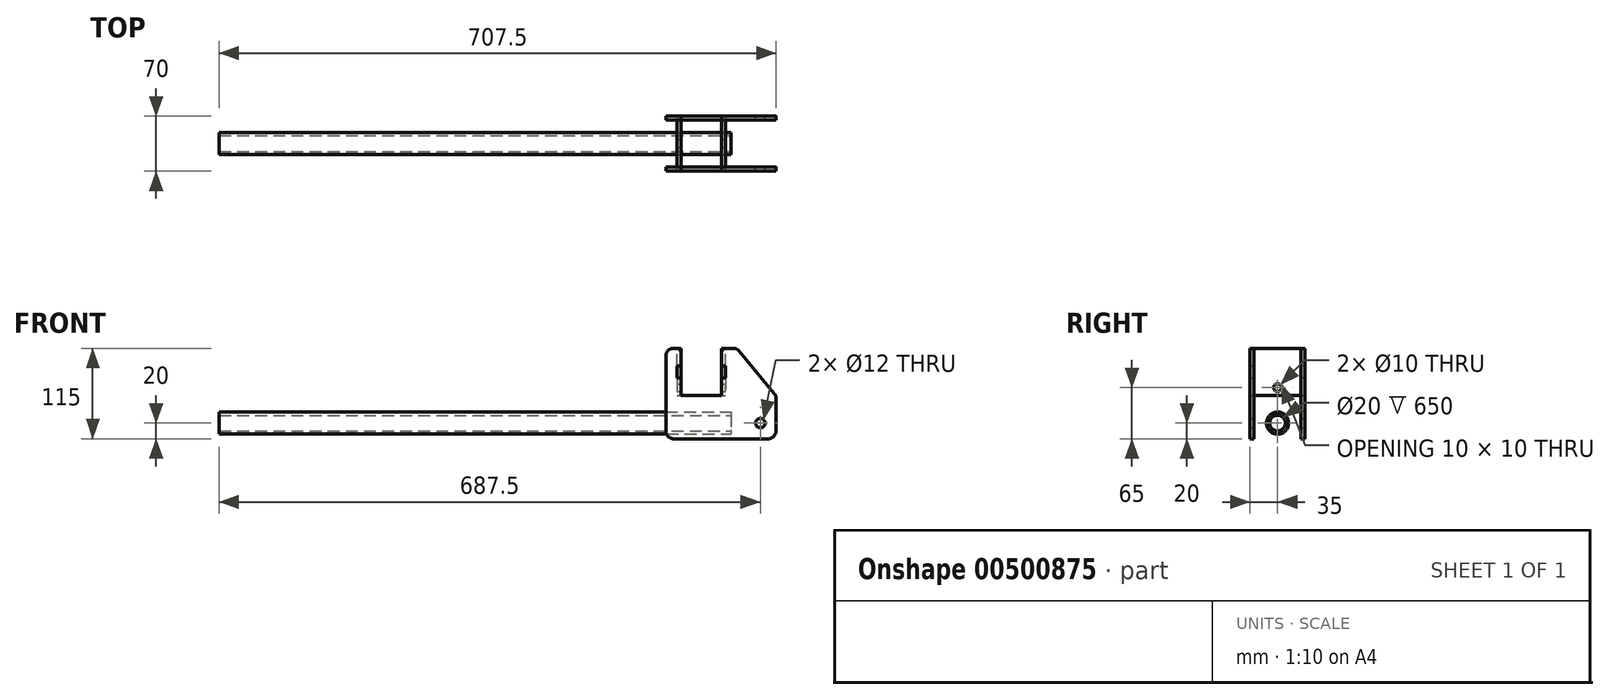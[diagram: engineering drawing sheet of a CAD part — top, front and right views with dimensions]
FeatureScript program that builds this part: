
annotation { "Feature Type Name" : "Feature", "Feature Type Description" : "" }
export const myFeature = defineFeature(function(context is Context, id is Id, definition is map)
    precondition{}
    {
        {
            var Q0;
            Q0=qCreatedBy(makeId("Front.planeOp"),FACE);
            var sketch = newSketch(context, id + "F0", { "sketchPlane" : qUnion([Q0])});
            skLineSegment(sketch, "E0", {"start": v(10, 0) * mm, "end": v(130, 0) * mm});
            skLineSegment(sketch, "E1", {"start": v(0, 10) * mm, "end": v(0, 105) * mm});
            skLineSegment(sketch, "E2", {"start": v(10, 115) * mm, "end": v(14, 115) * mm});
            skLineSegment(sketch, "E3", {"start": v(93, 111.4) * mm, "end": v(137.68, 57.78) * mm});
            skLineSegment(sketch, "E4", {"start": v(140, 51.38) * mm, "end": v(140, 10) * mm});
            skPoint(sketch, "E5", {"position": v(19, 55) * mm});
            skPoint(sketch, "E6", {"position": v(45, 115) * mm});
            skLineSegment(sketch, "E7", {"start": v(19, 55) * mm, "end": v(19, 110) * mm});
            skLineSegment(sketch, "E8", {"start": v(19, 55) * mm, "end": v(71, 55) * mm});
            skLineSegment(sketch, "E9", {"start": v(71, 55) * mm, "end": v(71, 110) * mm});
            skPoint(sketch, "E10", {"position": v(19, 85) * mm});
            skLineSegment(sketch, "E11", {"start": v(19, 85) * mm, "end": v(19, 92.5) * mm});
            skLineSegment(sketch, "E12", {"start": v(19, 92.5) * mm, "end": v(14, 92.5) * mm});
            skLineSegment(sketch, "E13", {"start": v(14, 92.5) * mm, "end": v(14, 77.5) * mm});
            skLineSegment(sketch, "E14", {"start": v(14, 77.5) * mm, "end": v(19, 77.5) * mm});
            skLineSegment(sketch, "E15", {"start": v(45, 115) * mm, "end": v(45, 55) * mm, "construction": true});
            skLineSegment(sketch, "E16.MirrorCS", {"start": v(71, 92.5) * mm, "end": v(76, 92.5) * mm});
            skLineSegment(sketch, "E17.MirrorCS", {"start": v(76, 92.5) * mm, "end": v(76, 77.5) * mm});
            skLineSegment(sketch, "E18.MirrorCS", {"start": v(76, 77.5) * mm, "end": v(71, 77.5) * mm});
            skPoint(sketch, "E19.visualSharp", {"position": v(90, 115) * mm});
            skArc(sketch, "E19.filletArc", {"start": v(93, 111.4) * mm, "mid": v(89.56, 114.06) * mm, "end": v(85.32, 115) * mm});
            skPoint(sketch, "E20.visualSharp", {"position": v(0, 115) * mm});
            skArc(sketch, "E20.filletArc", {"start": v(10, 115) * mm, "mid": v(2.93, 112.07) * mm, "end": v(0, 105) * mm});
            skPoint(sketch, "E21.visualSharp", {"position": v(0, 0) * mm});
            skArc(sketch, "E21.filletArc", {"start": v(0, 10) * mm, "mid": v(2.93, 2.93) * mm, "end": v(10, 0) * mm});
            skPoint(sketch, "E22.visualSharp", {"position": v(140, 0) * mm});
            skArc(sketch, "E22.filletArc", {"start": v(130, 0) * mm, "mid": v(137.07, 2.93) * mm, "end": v(140, 10) * mm});
            skPoint(sketch, "E23.visualSharp", {"position": v(140, 55) * mm});
            skArc(sketch, "E23.filletArc", {"start": v(140, 51.38) * mm, "mid": v(139.4, 54.78) * mm, "end": v(137.68, 57.78) * mm});
            skPoint(sketch, "E24", {"position": v(120, 20) * mm});
            skCircle(sketch, "E25", {"center": v(120, 20) * mm, "radius": 6 * mm});
            skLineSegment(sketch, "E26.trimOffspring", {"start": v(76, 115) * mm, "end": v(85.32, 115) * mm});
            skPoint(sketch, "E27.visualSharp", {"position": v(19, 115) * mm});
            skArc(sketch, "E27.filletArc", {"start": v(19, 110) * mm, "mid": v(17.54, 113.54) * mm, "end": v(14, 115) * mm});
            skPoint(sketch, "E28.visualSharp", {"position": v(71, 115) * mm});
            skArc(sketch, "E28.filletArc", {"start": v(76, 115) * mm, "mid": v(72.46, 113.54) * mm, "end": v(71, 110) * mm});
            skSolve(sketch);
        }
        {
            var Q0;
            Q0=makeQuery(id+"F0.imprint","IMPRINT",FACE,{"disambiguationData":[TD([[makeQuery(id+"F0.imprint","IMPRINT",EDGE,{"derivedFrom":sQuery(id+"F0.wireOp",EDGE,"E0")}),1.0]])]});
            extrude(context, id + "F1", {"entities" : qUnion([Q0]), "depth" : 5 * mm});
        }
        {
            var Q0;
            Q0=makeQuery(id+"F1.opExtrude","SWEPT_FACE",FACE,{"disambiguationData":[OSD([sQuery(id+"F0.wireOp",EDGE,"E17.MirrorCS")])]});
            var sketch = newSketch(context, id + "F2", { "sketchPlane" : qUnion([Q0])});
            skLineSegment(sketch, "E29.0", {"start": v(5, 92.5) * mm, "end": v(5, 77.5) * mm});
            skLineSegment(sketch, "E30.0.1", {"start": v(0, 92.5) * mm, "end": v(5, 92.5) * mm});
            skLineSegment(sketch, "E30.0.3", {"start": v(5, 92.5) * mm, "end": v(0, 92.5) * mm});
            skLineSegment(sketch, "E31.0", {"start": v(5, 77.5) * mm, "end": v(0, 77.5) * mm});
            skLineSegment(sketch, "E32", {"start": v(0, 92.5) * mm, "end": v(0, 115) * mm});
            skLineSegment(sketch, "E33", {"start": v(0, 115) * mm, "end": v(-60, 115) * mm});
            skLineSegment(sketch, "E34", {"start": v(-60, 115) * mm, "end": v(-60, 55) * mm});
            skLineSegment(sketch, "E35", {"start": v(-60, 55) * mm, "end": v(0, 55) * mm});
            skLineSegment(sketch, "E36", {"start": v(0, 55) * mm, "end": v(0, 77.5) * mm});
            skLineSegment(sketch, "E37", {"start": v(-30, 115) * mm, "end": v(-30, 55) * mm, "construction": true});
            skLineSegment(sketch, "E38.MirrorCS", {"start": v(-65, 92.5) * mm, "end": v(-65, 77.5) * mm});
            skLineSegment(sketch, "E39.MirrorCS", {"start": v(-65, 77.5) * mm, "end": v(-60, 77.5) * mm});
            skLineSegment(sketch, "E40.MirrorCS", {"start": v(-65, 92.5) * mm, "end": v(-60, 92.5) * mm});
            skSolve(sketch);
        }
        {
            var Q0;
            Q0=qSketchRegion(id+"F2",true);
            extrude(context, id + "F3", {"entities" : qUnion([Q0]), "depth" : 5 * mm});
        }
        {
            var Q0;
            Q0=makeQuery(id+"F3.opExtrude","CAP_FACE",FACE,{"disambiguationData":[OSD([sQuery(id+"F2.wireOp",EDGE,"E29.0"),sQuery(id+"F2.wireOp",EDGE,"E30.0.3"),sQuery(id+"F2.wireOp",EDGE,"E31.0"),sQuery(id+"F2.wireOp",EDGE,"E32"),sQuery(id+"F2.wireOp",EDGE,"E33"),sQuery(id+"F2.wireOp",EDGE,"E34"),sQuery(id+"F2.wireOp",EDGE,"E35"),sQuery(id+"F2.wireOp",EDGE,"E36"),sQuery(id+"F2.wireOp",EDGE,"E38.MirrorCS"),sQuery(id+"F2.wireOp",EDGE,"E39.MirrorCS"),sQuery(id+"F2.wireOp",EDGE,"E40.MirrorCS")])],"isStart":true});
            var sketch = newSketch(context, id + "F4", { "sketchPlane" : qUnion([Q0])});
            skPoint(sketch, "E41", {"position": v(30, 65) * mm});
            skPoint(sketch, "E41.positionSnap0", {"position": v(30, 55) * mm});
            skCircle(sketch, "E42", {"center": v(30, 65) * mm, "radius": 5 * mm});
            skSolve(sketch);
        }
        {
            var Q0;
            Q0 = qSketchRegion(id + "F4", true);
            extrude(context, id + "F5", {"entities" : qUnion([Q0]), "operationType" : NewBodyOperationType.REMOVE, "oppositeDirection" : true, "depth" : 25 * mm, "offsetDistance" : 25 * mm});
        }
        {
            var Q0;
            Q0=makeQuery(id+"F1.opExtrude","CAP_FACE",FACE,{"disambiguationData":[OSD([sQuery(id+"F0.wireOp",EDGE,"E0"),sQuery(id+"F0.wireOp",EDGE,"E1"),sQuery(id+"F0.wireOp",EDGE,"E2"),sQuery(id+"F0.wireOp",EDGE,"E3"),sQuery(id+"F0.wireOp",EDGE,"E4"),sQuery(id+"F0.wireOp",EDGE,"E7"),sQuery(id+"F0.wireOp",EDGE,"E8"),sQuery(id+"F0.wireOp",EDGE,"E9"),sQuery(id+"F0.wireOp",EDGE,"E12"),sQuery(id+"F0.wireOp",EDGE,"E13"),sQuery(id+"F0.wireOp",EDGE,"E14"),sQuery(id+"F0.wireOp",EDGE,"E16.MirrorCS"),sQuery(id+"F0.wireOp",EDGE,"E17.MirrorCS"),sQuery(id+"F0.wireOp",EDGE,"E18.MirrorCS"),sQuery(id+"F0.wireOp",EDGE,"E19.filletArc"),sQuery(id+"F0.wireOp",EDGE,"E20.filletArc"),sQuery(id+"F0.wireOp",EDGE,"E21.filletArc"),sQuery(id+"F0.wireOp",EDGE,"E22.filletArc"),sQuery(id+"F0.wireOp",EDGE,"E23.filletArc"),sQuery(id+"F0.wireOp",EDGE,"E25"),sQuery(id+"F0.wireOp",EDGE,"E26.trimOffspring"),sQuery(id+"F0.wireOp",EDGE,"E27.filletArc"),sQuery(id+"F0.wireOp",EDGE,"E28.filletArc")])],"isStart":true});
            cPlane(context, id + "F6", {"entities" : qUnion([Q0]), "cplaneType" : CPlaneType.OFFSET, "offset" : 10 * mm, "width" : 150 * mm, "height" : 150 * mm});
        }
        {
            var Q0;
            Q0=qCreatedBy(id+"F6.planeOp",FACE);
            var sketch = newSketch(context, id + "F7", { "sketchPlane" : qUnion([Q0])});
            skCircle(sketch, "E43.0", {"center": v(-120, 20) * mm, "radius": 6 * mm, "construction": true});
            skCircle(sketch, "E44", {"center": v(-120, 20) * mm, "radius": 26 * mm});
            skLineSegment(sketch, "E45.bottom", {"start": v(-82.5, 55) * mm, "end": v(-157.5, 55) * mm});
            skLineSegment(sketch, "E45.top", {"start": v(-82.5, -15) * mm, "end": v(-157.5, -15) * mm});
            skLineSegment(sketch, "E45.left", {"start": v(-82.5, 55) * mm, "end": v(-82.5, -15) * mm});
            skLineSegment(sketch, "E45.right", {"start": v(-157.5, 55) * mm, "end": v(-157.5, -15) * mm});
            skSolve(sketch);
        }
        {
            var Q0;
            Q0 = qSketchRegion(id + "F7", true);
            extrude(context, id + "F8", {"entities" : qUnion([Q0]), "depth" : 40 * mm, "offsetDistance" : 25 * mm});
        }
        {
            var Q0;
            Q0=makeQuery(id+"F8.opExtrude","SWEPT_FACE",FACE,{"disambiguationData":[OSD([sQuery(id+"F7.wireOp",EDGE,"E45.bottom")])]});
            var sketch = newSketch(context, id + "F9", { "sketchPlane" : qUnion([Q0])});
            skLineSegment(sketch, "E46", {"start": v(82.5, 15) * mm, "end": v(157.5, 15) * mm});
            skLineSegment(sketch, "E47", {"start": v(157.5, 15) * mm, "end": v(157.5, 45) * mm});
            skLineSegment(sketch, "E48", {"start": v(157.5, 45) * mm, "end": v(82.5, 45) * mm});
            skLineSegment(sketch, "E49", {"start": v(87.5, 15) * mm, "end": v(87.5, 45) * mm});
            skSolve(sketch);
        }
        {
            var Q0;
            Q0 = qSketchRegion(id + "F9", true);
            extrude(context, id + "F10", {"entities" : qUnion([Q0]), "operationType" : NewBodyOperationType.REMOVE, "oppositeDirection" : true, "depth" : 70 * mm, "offsetDistance" : 25 * mm});
        }
        {
            var Q0;
            Q0=makeQuery(id+"F8.opExtrude","SWEPT_EDGE",EDGE,{"disambiguationData":[OSD([sQuery(id+"F7.wireOp",EDGE,"E45.top"),sQuery(id+"F7.wireOp",EDGE,"E45.left")])]});
            var Q1;
            Q1=makeQuery(id+"F8.opExtrude","SWEPT_EDGE",EDGE,{"disambiguationData":[OSD([sQuery(id+"F7.wireOp",EDGE,"E45.bottom"),sQuery(id+"F7.wireOp",EDGE,"E45.left")])]});
            fillet(context, id + "F11", {"entities" : qUnion([Q0, Q1]), "radius" : 15 * mm, "tangentPropagation" : true, "allowEdgeOverflow" : false});
        }
        {
            var Q0;
            {var subQ0=sQuery(id+"F7.wireOp",EDGE,"E45.right");var subQ1=sQuery(id+"F7.wireOp",EDGE,"E45.bottom");Q0=makeQuery(id+"F10.boolean.opBoolean","SPLIT",EDGE,{"disambiguationData":[TD([makeQuery(id+"F10.opExtrude","SWEPT_FACE",FACE,{"disambiguationData":[OSD([sQuery(id+"F9.wireOp",EDGE,"E48")])]})])],"derivedFrom":makeQuery(id+"F8.opExtrude","SWEPT_EDGE",EDGE,{"disambiguationData":[OSD([subQ1,subQ0])]})});}
            var Q1;
            {var subQ0=sQuery(id+"F7.wireOp",EDGE,"E45.right");var subQ1=sQuery(id+"F7.wireOp",EDGE,"E45.bottom");Q1=makeQuery(id+"F10.boolean.opBoolean","SPLIT",EDGE,{"disambiguationData":[TD([makeQuery(id+"F10.opExtrude","SWEPT_FACE",FACE,{"disambiguationData":[OSD([sQuery(id+"F9.wireOp",EDGE,"E46")])]})])],"derivedFrom":makeQuery(id+"F8.opExtrude","SWEPT_EDGE",EDGE,{"disambiguationData":[OSD([subQ1,subQ0])]})});}
            var Q2;
            {var subQ0=sQuery(id+"F7.wireOp",EDGE,"E45.right");var subQ1=sQuery(id+"F7.wireOp",EDGE,"E45.top");Q2=makeQuery(id+"F10.boolean.opBoolean","SPLIT",EDGE,{"disambiguationData":[TD([makeQuery(id+"F10.opExtrude","SWEPT_FACE",FACE,{"disambiguationData":[OSD([sQuery(id+"F9.wireOp",EDGE,"E48")])]})])],"derivedFrom":makeQuery(id+"F8.opExtrude","SWEPT_EDGE",EDGE,{"disambiguationData":[OSD([subQ1,subQ0])]})});}
            var Q3;
            {var subQ0=sQuery(id+"F7.wireOp",EDGE,"E45.right");var subQ1=sQuery(id+"F7.wireOp",EDGE,"E45.top");Q3=makeQuery(id+"F10.boolean.opBoolean","SPLIT",EDGE,{"disambiguationData":[TD([makeQuery(id+"F10.opExtrude","SWEPT_FACE",FACE,{"disambiguationData":[OSD([sQuery(id+"F9.wireOp",EDGE,"E46")])]})])],"derivedFrom":makeQuery(id+"F8.opExtrude","SWEPT_EDGE",EDGE,{"disambiguationData":[OSD([subQ1,subQ0])]})});}
            fillet(context, id + "F12", {"entities" : qUnion([Q0, Q1, Q2, Q3]), "radius" : 5 * mm, "tangentPropagation" : true, "allowEdgeOverflow" : false});
        }
        {
            var Q0;
            Q0=makeQuery(id+"F8.opExtrude","SWEPT_FACE",FACE,{"disambiguationData":[OSD([sQuery(id+"F7.wireOp",EDGE,"E45.left")])]});
            var sketch = newSketch(context, id + "F13", { "sketchPlane" : qUnion([Q0])});
            skCircle(sketch, "E50", {"center": v(-30, 20) * mm, "radius": 14 * mm});
            skPoint(sketch, "E50.centerSnap0", {"position": v(-50, 20) * mm});
            skPoint(sketch, "E50.centerSnap1", {"position": v(-30, 40) * mm});
            skSolve(sketch);
        }
        {
            var Q0;
            Q0 = qSketchRegion(id + "F13", true);
            extrude(context, id + "F14", {"entities" : qUnion([Q0]), "operationType" : NewBodyOperationType.REMOVE, "oppositeDirection" : true, "depth" : 25 * mm, "offsetDistance" : 25 * mm});
        }
        {
            var Q0;
            Q0=makeQuery(id+"F8.opExtrude","SWEPT_FACE",FACE,{"disambiguationData":[OSD([sQuery(id+"F7.wireOp",EDGE,"E45.left")])]});
            var sketch = newSketch(context, id + "F15", { "sketchPlane" : qUnion([Q0])});
            skCircle(sketch, "E51.0", {"center": v(-30, 20) * mm, "radius": 14 * mm});
            skCircle(sketch, "E52", {"center": v(-30, 20) * mm, "radius": 10 * mm});
            skSolve(sketch);
        }
        {
            var Q0;
            Q0 = qSketchRegion(id + "F15", true);
            extrude(context, id + "F16", {"entities" : qUnion([Q0]), "depth" : 650 * mm, "offsetDistance" : 25 * mm});
        }
        {
            var Q0;
            Q0=makeQuery(id+"F1.opExtrude","CAP_FACE",FACE,{"disambiguationData":[OSD([sQuery(id+"F0.wireOp",EDGE,"E0"),sQuery(id+"F0.wireOp",EDGE,"E1"),sQuery(id+"F0.wireOp",EDGE,"E2"),sQuery(id+"F0.wireOp",EDGE,"E3"),sQuery(id+"F0.wireOp",EDGE,"E4"),sQuery(id+"F0.wireOp",EDGE,"E7"),sQuery(id+"F0.wireOp",EDGE,"E8"),sQuery(id+"F0.wireOp",EDGE,"E9"),sQuery(id+"F0.wireOp",EDGE,"E12"),sQuery(id+"F0.wireOp",EDGE,"E13"),sQuery(id+"F0.wireOp",EDGE,"E14"),sQuery(id+"F0.wireOp",EDGE,"E16.MirrorCS"),sQuery(id+"F0.wireOp",EDGE,"E17.MirrorCS"),sQuery(id+"F0.wireOp",EDGE,"E18.MirrorCS"),sQuery(id+"F0.wireOp",EDGE,"E19.filletArc"),sQuery(id+"F0.wireOp",EDGE,"E20.filletArc"),sQuery(id+"F0.wireOp",EDGE,"E21.filletArc"),sQuery(id+"F0.wireOp",EDGE,"E22.filletArc"),sQuery(id+"F0.wireOp",EDGE,"E23.filletArc"),sQuery(id+"F0.wireOp",EDGE,"E25"),sQuery(id+"F0.wireOp",EDGE,"E26.trimOffspring"),sQuery(id+"F0.wireOp",EDGE,"E27.filletArc"),sQuery(id+"F0.wireOp",EDGE,"E28.filletArc")])],"isStart":true});
            var sketch = newSketch(context, id + "F17", { "sketchPlane" : qUnion([Q0])});
            skCircle(sketch, "E53", {"center": v(-120, 20) * mm, "radius": 2.5 * mm});
            skSolve(sketch);
        }
        {
            var Q0;
            Q0=makeQuery(id+"F17.imprint","IMPRINT",FACE,{"disambiguationData":[TD([[makeQuery(id+"F17.imprint","IMPRINT",EDGE,{"derivedFrom":sQuery(id+"F17.wireOp",EDGE,"E53")}),1.0]])]});
            extrude(context, id + "F18", {"entities" : qUnion([Q0]), "depth" : 60 * mm, "offsetDistance" : 25 * mm});
        }
        {
            var Q0;
            Q0=makeQuery(id+"F8.opExtrude","SWEPT_BODY",BODY,{"disambiguationData":[OSD([sQuery(id+"F7.wireOp",EDGE,"E44"),sQuery(id+"F7.wireOp",EDGE,"E45.bottom"),sQuery(id+"F7.wireOp",EDGE,"E45.top"),sQuery(id+"F7.wireOp",EDGE,"E45.left"),sQuery(id+"F7.wireOp",EDGE,"E45.right")])]});
            deleteBodies(context, id + "F19", {"entities" : qUnion([Q0])});
        }
        {
            var Q0;
            Q0=makeQuery(id+"F18.opExtrude","SWEPT_BODY",BODY,{"disambiguationData":[OSD([sQuery(id+"F17.wireOp",EDGE,"E53")])]});
            deleteBodies(context, id + "F20", {"entities" : qUnion([Q0])});
        }
        {
            var Q0;
            Q0=makeQuery(id+"F1.opExtrude","SWEPT_BODY",BODY,{"disambiguationData":[OSD([sQuery(id+"F0.wireOp",EDGE,"E0"),sQuery(id+"F0.wireOp",EDGE,"E1"),sQuery(id+"F0.wireOp",EDGE,"E2"),sQuery(id+"F0.wireOp",EDGE,"E3"),sQuery(id+"F0.wireOp",EDGE,"E4"),sQuery(id+"F0.wireOp",EDGE,"E7"),sQuery(id+"F0.wireOp",EDGE,"E8"),sQuery(id+"F0.wireOp",EDGE,"E9"),sQuery(id+"F0.wireOp",EDGE,"E12"),sQuery(id+"F0.wireOp",EDGE,"E13"),sQuery(id+"F0.wireOp",EDGE,"E14"),sQuery(id+"F0.wireOp",EDGE,"E16.MirrorCS"),sQuery(id+"F0.wireOp",EDGE,"E17.MirrorCS"),sQuery(id+"F0.wireOp",EDGE,"E18.MirrorCS"),sQuery(id+"F0.wireOp",EDGE,"E19.filletArc"),sQuery(id+"F0.wireOp",EDGE,"E20.filletArc"),sQuery(id+"F0.wireOp",EDGE,"E21.filletArc"),sQuery(id+"F0.wireOp",EDGE,"E22.filletArc"),sQuery(id+"F0.wireOp",EDGE,"E23.filletArc"),sQuery(id+"F0.wireOp",EDGE,"E25"),sQuery(id+"F0.wireOp",EDGE,"E26.trimOffspring"),sQuery(id+"F0.wireOp",EDGE,"E27.filletArc"),sQuery(id+"F0.wireOp",EDGE,"E28.filletArc")])]});
            transform(context, id + "F21", {"entities" : qUnion([Q0]), "transformType" : TransformType.TRANSLATION_3D, "dx" : 0 * mm, "dy" : 65 * mm, "dz" : 0 * mm, "makeCopy" : true});
        }
        {
            var Q0;
            Q0=makeQuery(id+"F3.opExtrude","SWEPT_BODY",BODY,{"disambiguationData":[OSD([sQuery(id+"F2.wireOp",EDGE,"E29.0"),sQuery(id+"F2.wireOp",EDGE,"E30.0.3"),sQuery(id+"F2.wireOp",EDGE,"E31.0"),sQuery(id+"F2.wireOp",EDGE,"E32"),sQuery(id+"F2.wireOp",EDGE,"E33"),sQuery(id+"F2.wireOp",EDGE,"E34"),sQuery(id+"F2.wireOp",EDGE,"E35"),sQuery(id+"F2.wireOp",EDGE,"E36"),sQuery(id+"F2.wireOp",EDGE,"E38.MirrorCS"),sQuery(id+"F2.wireOp",EDGE,"E39.MirrorCS"),sQuery(id+"F2.wireOp",EDGE,"E40.MirrorCS")])]});
            transform(context, id + "F22", {"entities" : qUnion([Q0]), "transformType" : TransformType.TRANSLATION_3D, "dx" : -57 * mm, "dy" : 0 * mm, "dz" : 0 * mm, "makeCopy" : true});
        }
    });
